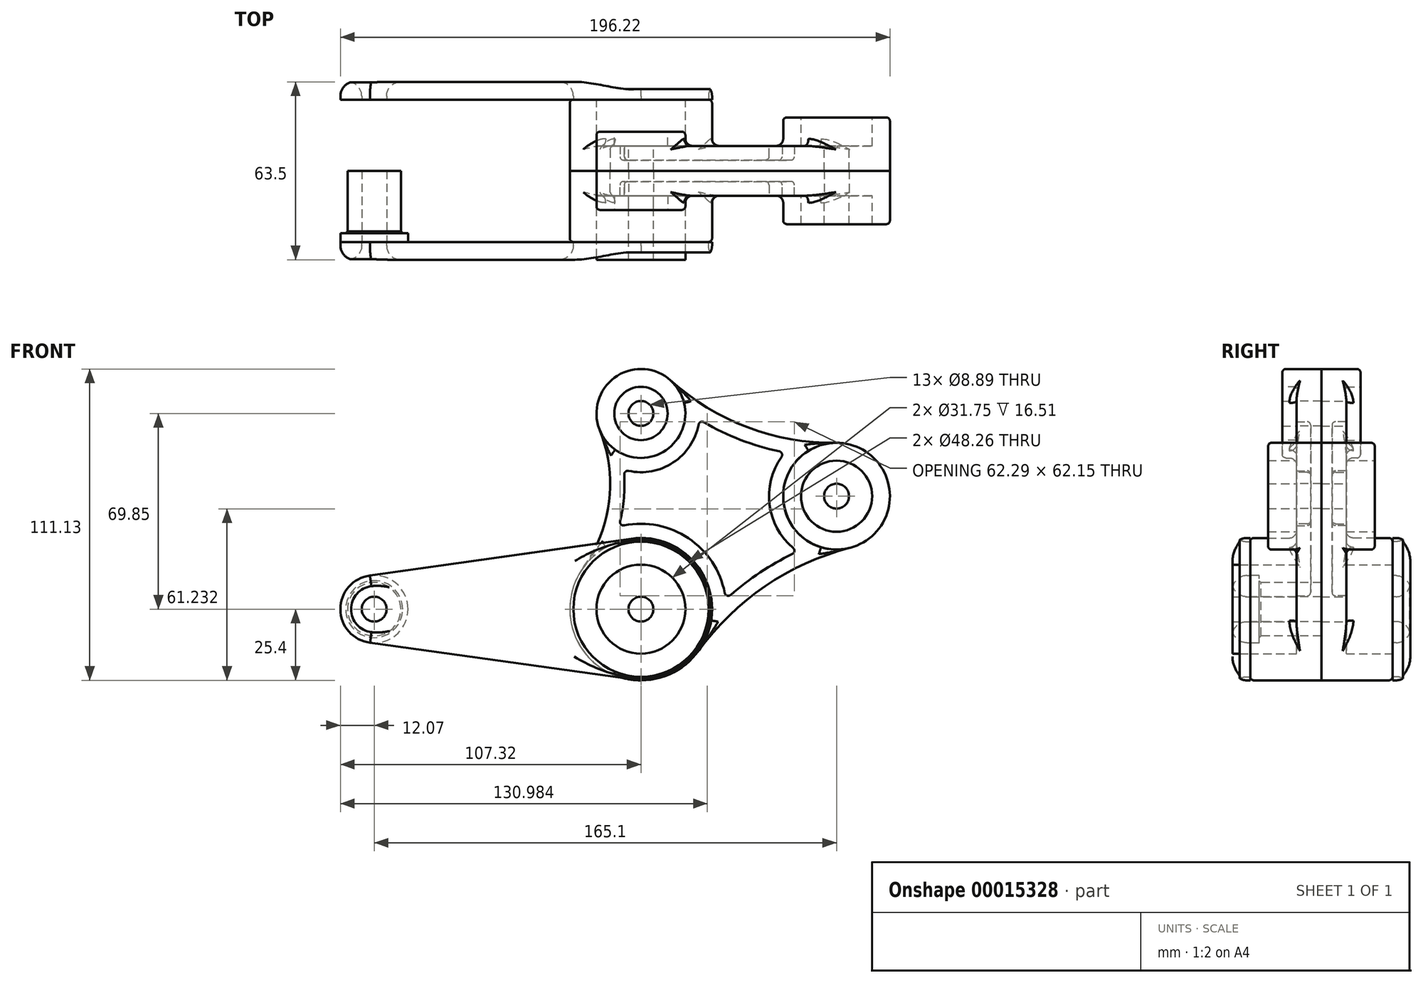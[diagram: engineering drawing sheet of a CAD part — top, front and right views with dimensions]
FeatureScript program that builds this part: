
annotation { "Feature Type Name" : "Feature", "Feature Type Description" : "" }
export const myFeature = defineFeature(function(context is Context, id is Id, definition is map)
    precondition{}
    {
        {
            var Q0;
            Q0=qCreatedBy(makeId("Front.planeOp"),FACE);
            var sketch = newSketch(context, id + "F0", { "sketchPlane" : qUnion([Q0])});
            skCircle(sketch, "E0", {"center": v(0, 0) * mm, "radius": 25.4 * mm});
            skCircle(sketch, "E1", {"center": v(0, 69.85) * mm, "radius": 15.88 * mm});
            skCircle(sketch, "E2", {"center": v(69.85, 40.33) * mm, "radius": 19.05 * mm});
            skLineSegment(sketch, "E3", {"start": v(0, 0) * mm, "end": v(69.85, 40.33) * mm, "construction": true});
            skLineSegment(sketch, "E4", {"start": v(0, 0) * mm, "end": v(74.27, 0) * mm, "construction": true});
            skArc(sketch, "E5", {"start": v(-20.58, 14.89) * mm, "mid": v(-11.3, 38.61) * mm, "end": v(-14.7, 63.85) * mm});
            skArc(sketch, "E6", {"start": v(74.6, 21.88) * mm, "mid": v(44.37, 8.2) * mm, "end": v(20.56, -14.91) * mm});
            skArc(sketch, "E7", {"start": v(10.64, 81.63) * mm, "mid": v(38.02, 64.93) * mm, "end": v(69.6, 59.38) * mm});
            skSolve(sketch);
        }
        {
            var Q0;
            {var subQ0=sQuery(id+"F0.wireOp",EDGE,"E0");var subQ1=sQuery(id+"F0.wireOp",EDGE,"E6");var subQ3=sQuery(id+"F0.wireOp",EDGE,"E5");var subQ4=makeQuery(id+"F0.imprint","INTERSECT",VERTEX,{"derivedFrom":[subQ0,subQ3]});var subQ6=sQuery(id+"F0.wireOp",EDGE,"E1");var subQ9=makeQuery(id+"F0.imprint","INTERSECT",VERTEX,{"derivedFrom":[subQ6,subQ3]});var subQ11=sQuery(id+"F0.wireOp",EDGE,"E2");var subQ13=makeQuery(id+"F0.imprint","INTERSECT",VERTEX,{"derivedFrom":[subQ11,subQ1]});var subQ14=makeQuery(id+"F0.imprint","IMPRINT",EDGE,{"disambiguationData":[TD([[subQ13,1.0]])],"derivedFrom":subQ11});Q0=qUnion([makeQuery(id+"F0.imprint","IMPRINT",FACE,{"disambiguationData":[TD([[makeQuery(id+"F0.imprint","IMPRINT",EDGE,{"disambiguationData":[TD([[subQ4,-1.0]])],"derivedFrom":subQ0}),1.0]])]}),makeQuery(id+"F0.imprint","IMPRINT",FACE,{"disambiguationData":[TD([[makeQuery(id+"F0.imprint","IMPRINT",EDGE,{"disambiguationData":[TD([[subQ9,1.0]])],"derivedFrom":subQ6}),1.0]])]}),makeQuery(id+"F0.imprint","IMPRINT",FACE,{"disambiguationData":[TD([[subQ14,1.0]])]}),makeQuery(id+"F0.imprint","IMPRINT",FACE,{"disambiguationData":[TD([[makeQuery(id+"F0.imprint","IMPRINT",EDGE,{"derivedFrom":subQ3}),-1.0]])]})]);}
            extrude(context, id + "F1", {"entities" : qUnion([Q0]), "depth" : 8.9 * mm});
        }
        {
            var Q0;
            {var subQ0=sQuery(id+"F0.wireOp",EDGE,"E1");var subQ2=makeQuery(id+"F0.imprint","INTERSECT",VERTEX,{"derivedFrom":[subQ0,sQuery(id+"F0.wireOp",EDGE,"E5")]});Q0=makeQuery(id+"F0.imprint","IMPRINT",FACE,{"disambiguationData":[TD([[makeQuery(id+"F0.imprint","IMPRINT",EDGE,{"disambiguationData":[TD([[subQ2,1.0]])],"derivedFrom":subQ0}),1.0]])]});}
            extrude(context, id + "F2", {"entities" : qUnion([Q0]), "operationType" : NewBodyOperationType.ADD, "depth" : 13.97 * mm});
        }
        {
            var Q0;
            {var subQ0=sQuery(id+"F0.wireOp",EDGE,"E2");var subQ2=makeQuery(id+"F0.imprint","INTERSECT",VERTEX,{"derivedFrom":[subQ0,sQuery(id+"F0.wireOp",EDGE,"E6")]});Q0=makeQuery(id+"F0.imprint","IMPRINT",FACE,{"disambiguationData":[TD([[makeQuery(id+"F0.imprint","IMPRINT",EDGE,{"disambiguationData":[TD([[subQ2,1.0]])],"derivedFrom":subQ0}),1.0]])]});}
            extrude(context, id + "F3", {"entities" : qUnion([Q0]), "operationType" : NewBodyOperationType.ADD, "depth" : 19.05 * mm});
        }
        {
            var Q0;
            {var subQ0=sQuery(id+"F0.wireOp",EDGE,"E0");var subQ2=makeQuery(id+"F0.imprint","INTERSECT",VERTEX,{"derivedFrom":[subQ0,sQuery(id+"F0.wireOp",EDGE,"E5")]});Q0=makeQuery(id+"F0.imprint","IMPRINT",FACE,{"disambiguationData":[TD([[makeQuery(id+"F0.imprint","IMPRINT",EDGE,{"disambiguationData":[TD([[subQ2,-1.0]])],"derivedFrom":subQ0}),1.0]])]});}
            extrude(context, id + "F4", {"entities" : qUnion([Q0]), "operationType" : NewBodyOperationType.ADD, "depth" : 25.4 * mm});
        }
        {
            var Q0;
            Q0=makeQuery(id+"F1.opExtrude","CAP_FACE",FACE,{"disambiguationData":[OSD([sQuery(id+"F0.wireOp",EDGE,"E0"),sQuery(id+"F0.wireOp",EDGE,"E1"),sQuery(id+"F0.wireOp",EDGE,"E2"),sQuery(id+"F0.wireOp",EDGE,"E5"),sQuery(id+"F0.wireOp",EDGE,"E6"),sQuery(id+"F0.wireOp",EDGE,"E7")])],"isStart":false});
            var sketch = newSketch(context, id + "F5", { "sketchPlane" : qUnion([Q0])});
            skCircle(sketch, "E8.0", {"center": v(0, 69.85) * mm, "radius": 20.96 * mm});
            skCircle(sketch, "E9.0", {"center": v(69.85, 40.33) * mm, "radius": 24.13 * mm});
            skCircle(sketch, "E10.0", {"center": v(0, 0) * mm, "radius": 30.48 * mm});
            skArc(sketch, "E11.0", {"start": v(-16.46, 11.91) * mm, "mid": v(-6.25, 38) * mm, "end": v(-10, 65.77) * mm});
            skArc(sketch, "E12.0", {"start": v(7.23, 77.86) * mm, "mid": v(36.23, 60.18) * mm, "end": v(69.67, 54.3) * mm});
            skArc(sketch, "E13.0", {"start": v(73.34, 26.8) * mm, "mid": v(41.51, 12.4) * mm, "end": v(16.45, -11.93) * mm});
            skSolve(sketch);
        }
        {
            var Q0;
            {var subQ5=sQuery(id+"F5.wireOp",EDGE,"E12.0");var subQ7=sQuery(id+"F5.wireOp",EDGE,"E8.0");var subQ8=makeQuery(id+"F5.imprint","INTERSECT",VERTEX,{"derivedFrom":[subQ7,subQ5]});Q0=makeQuery(id+"F5.imprint","IMPRINT",FACE,{"disambiguationData":[TD([[makeQuery(id+"F5.imprint","IMPRINT",EDGE,{"disambiguationData":[TD([[subQ8,1.0]])],"derivedFrom":subQ7}),-1.0]])]});}
            extrude(context, id + "F6", {"entities" : qUnion([Q0]), "operationType" : NewBodyOperationType.REMOVE, "oppositeDirection" : true, "depth" : 5.08 * mm});
        }
        {
            var Q0;
            Q0=makeQuery(id+"F4.opExtrude","CAP_FACE",FACE,{"disambiguationData":[OSD([sQuery(id+"F0.wireOp",EDGE,"E0")])],"isStart":false});
            var sketch = newSketch(context, id + "F7", { "sketchPlane" : qUnion([Q0])});
            skCircle(sketch, "E14", {"center": v(0, 0) * mm, "radius": 15.88 * mm});
            skCircle(sketch, "E15.0", {"center": v(0, 69.85) * mm, "radius": 15.88 * mm, "construction": true});
            skCircle(sketch, "E15.1", {"center": v(69.85, 40.33) * mm, "radius": 19.05 * mm, "construction": true});
            skCircle(sketch, "E16", {"center": v(0, 69.85) * mm, "radius": 9.53 * mm});
            skCircle(sketch, "E17", {"center": v(69.85, 40.33) * mm, "radius": 12.7 * mm});
            skSolve(sketch);
        }
        {
            var Q0;
            Q0=makeQuery(id+"F7.imprint","IMPRINT",FACE,{"disambiguationData":[TD([[makeQuery(id+"F7.imprint","IMPRINT",EDGE,{"derivedFrom":sQuery(id+"F7.wireOp",EDGE,"E14")}),1.0]])]});
            var Q1;
            Q1=makeQuery(id+"F7.imprint","IMPRINT",FACE,{"disambiguationData":[TD([[makeQuery(id+"F7.imprint","IMPRINT",EDGE,{"derivedFrom":sQuery(id+"F7.wireOp",EDGE,"E16")}),1.0]])]});
            var Q2;
            Q2=makeQuery(id+"F7.imprint","IMPRINT",FACE,{"disambiguationData":[TD([[makeQuery(id+"F7.imprint","IMPRINT",EDGE,{"derivedFrom":sQuery(id+"F7.wireOp",EDGE,"E17")}),1.0]])]});
            var Q3;
            Q3=makeQuery(id+"F1.opExtrude","CAP_FACE",FACE,{"disambiguationData":[OSD([sQuery(id+"F0.wireOp",EDGE,"E0"),sQuery(id+"F0.wireOp",EDGE,"E1"),sQuery(id+"F0.wireOp",EDGE,"E2"),sQuery(id+"F0.wireOp",EDGE,"E5"),sQuery(id+"F0.wireOp",EDGE,"E6"),sQuery(id+"F0.wireOp",EDGE,"E7")])],"isStart":false});
            extrude(context, id + "F8", {"entities" : qUnion([Q0, Q1, Q2]), "operationType" : NewBodyOperationType.REMOVE, "endBound" : BoundingType.UP_TO_SURFACE, "oppositeDirection" : true, "endBoundEntityFace" : qUnion([Q3]), "depth" : 25.4 * mm});
        }
        {
            var Q0;
            Q0=makeQuery(id+"F8.boolean.opBoolean","COPY",FACE,{"derivedFrom":makeQuery(id+"F8.opExtrude","CAP_FACE",FACE,{"disambiguationData":[OSD([sQuery(id+"F7.wireOp",EDGE,"E17")])],"isStart":false})});
            var sketch = newSketch(context, id + "F9", { "sketchPlane" : qUnion([Q0])});
            skCircle(sketch, "E18.0", {"center": v(0, 69.85) * mm, "radius": 9.53 * mm});
            skCircle(sketch, "E18.1", {"center": v(0, 0) * mm, "radius": 15.88 * mm});
            skCircle(sketch, "E18.2", {"center": v(69.85, 40.33) * mm, "radius": 12.7 * mm});
            skCircle(sketch, "E19", {"center": v(0, 0) * mm, "radius": 4.45 * mm});
            skCircle(sketch, "E20", {"center": v(0, 69.85) * mm, "radius": 4.45 * mm});
            skCircle(sketch, "E21", {"center": v(69.85, 40.33) * mm, "radius": 4.45 * mm});
            skSolve(sketch);
        }
        {
            var Q0;
            Q0=makeQuery(id+"F9.imprint","IMPRINT",FACE,{"disambiguationData":[TD([[makeQuery(id+"F9.imprint","IMPRINT",EDGE,{"derivedFrom":sQuery(id+"F9.wireOp",EDGE,"E20")}),1.0]])]});
            var Q1;
            Q1=makeQuery(id+"F9.imprint","IMPRINT",FACE,{"disambiguationData":[TD([[makeQuery(id+"F9.imprint","IMPRINT",EDGE,{"derivedFrom":sQuery(id+"F9.wireOp",EDGE,"E21")}),1.0]])]});
            var Q2;
            Q2=makeQuery(id+"F9.imprint","IMPRINT",FACE,{"disambiguationData":[TD([[makeQuery(id+"F9.imprint","IMPRINT",EDGE,{"derivedFrom":sQuery(id+"F9.wireOp",EDGE,"E19")}),1.0]])]});
            extrude(context, id + "F10", {"entities" : qUnion([Q0, Q1, Q2]), "operationType" : NewBodyOperationType.REMOVE, "endBound" : BoundingType.THROUGH_ALL, "oppositeDirection" : true, "depth" : 25.4 * mm});
        }
        {
            var Q0;
            Q0=makeQuery(id+"F6.boolean.opBoolean","COPY",FACE,{"derivedFrom":makeQuery(id+"F6.opExtrude","CAP_FACE",FACE,{"disambiguationData":[OSD([sQuery(id+"F5.wireOp",EDGE,"E8.0"),sQuery(id+"F5.wireOp",EDGE,"E9.0"),sQuery(id+"F5.wireOp",EDGE,"E10.0"),sQuery(id+"F5.wireOp",EDGE,"E11.0"),sQuery(id+"F5.wireOp",EDGE,"E12.0"),sQuery(id+"F5.wireOp",EDGE,"E13.0")])],"isStart":false})});
            var Q1;
            Q1=makeQuery(id+"F6.boolean.opBoolean","COPY",EDGE,{"derivedFrom":makeQuery(id+"F6.opExtrude","SWEPT_EDGE",EDGE,{"disambiguationData":[OSD([sQuery(id+"F5.wireOp",EDGE,"E8.0"),sQuery(id+"F5.wireOp",EDGE,"E11.0")])]})});
            var Q2;
            Q2=makeQuery(id+"F6.boolean.opBoolean","COPY",EDGE,{"derivedFrom":makeQuery(id+"F6.opExtrude","SWEPT_EDGE",EDGE,{"disambiguationData":[OSD([sQuery(id+"F5.wireOp",EDGE,"E8.0"),sQuery(id+"F5.wireOp",EDGE,"E12.0")])]})});
            var Q3;
            Q3=makeQuery(id+"F6.boolean.opBoolean","COPY",EDGE,{"derivedFrom":makeQuery(id+"F6.opExtrude","SWEPT_EDGE",EDGE,{"disambiguationData":[OSD([sQuery(id+"F5.wireOp",EDGE,"E9.0"),sQuery(id+"F5.wireOp",EDGE,"E12.0")])]})});
            var Q4;
            Q4=makeQuery(id+"F6.boolean.opBoolean","COPY",EDGE,{"derivedFrom":makeQuery(id+"F6.opExtrude","SWEPT_EDGE",EDGE,{"disambiguationData":[OSD([sQuery(id+"F5.wireOp",EDGE,"E9.0"),sQuery(id+"F5.wireOp",EDGE,"E13.0")])]})});
            var Q5;
            Q5=makeQuery(id+"F6.boolean.opBoolean","COPY",EDGE,{"derivedFrom":makeQuery(id+"F6.opExtrude","SWEPT_EDGE",EDGE,{"disambiguationData":[OSD([sQuery(id+"F5.wireOp",EDGE,"E10.0"),sQuery(id+"F5.wireOp",EDGE,"E13.0")])]})});
            var Q6;
            Q6=makeQuery(id+"F6.boolean.opBoolean","COPY",EDGE,{"derivedFrom":makeQuery(id+"F6.opExtrude","SWEPT_EDGE",EDGE,{"disambiguationData":[OSD([sQuery(id+"F5.wireOp",EDGE,"E10.0"),sQuery(id+"F5.wireOp",EDGE,"E11.0")])]})});
            var Q7;
            Q7=makeQuery(id+"F6.boolean.opBoolean","COPY",EDGE,{"derivedFrom":makeQuery(id+"F6.opExtrude","CAP_EDGE",EDGE,{"disambiguationData":[OSD([sQuery(id+"F5.wireOp",EDGE,"E10.0")])],"isStart":true})});
            var Q8;
            Q8=makeQuery(id+"F1.opExtrude","CAP_EDGE",EDGE,{"disambiguationData":[OSD([sQuery(id+"F0.wireOp",EDGE,"E7")])],"isStart":false});
            var Q9;
            Q9=makeQuery(id+"F1.opExtrude","CAP_EDGE",EDGE,{"disambiguationData":[OSD([sQuery(id+"F0.wireOp",EDGE,"E6")])],"isStart":false});
            var Q10;
            Q10=makeQuery(id+"F1.opExtrude","CAP_EDGE",EDGE,{"disambiguationData":[OSD([sQuery(id+"F0.wireOp",EDGE,"E5")])],"isStart":false});
            var Q11;
            Q11=makeQuery(id+"F4.opExtrude","CAP_EDGE",EDGE,{"disambiguationData":[OSD([sQuery(id+"F0.wireOp",EDGE,"E0")])],"isStart":false});
            var Q12;
            Q12=makeQuery(id+"F3.opExtrude","CAP_EDGE",EDGE,{"disambiguationData":[OSD([sQuery(id+"F0.wireOp",EDGE,"E2")])],"isStart":false});
            var Q13;
            Q13=makeQuery(id+"F2.opExtrude","CAP_EDGE",EDGE,{"disambiguationData":[OSD([sQuery(id+"F0.wireOp",EDGE,"E1")])],"isStart":false});
            fillet(context, id + "F11", {"entities" : qUnion([Q0, Q1, Q2, Q3, Q4, Q5, Q6, Q7, Q8, Q9, Q10, Q11, Q12, Q13]), "radius" : 1.27 * mm, "tangentPropagation" : true, "allowEdgeOverflow" : false});
        }
        {
            var Q0;
            {var subQ0=sQuery(id+"F0.wireOp",EDGE,"E2");Q0=makeQuery(id+"F3.boolean.opBoolean","INTERSECT",EDGE,{"derivedFrom":[makeQuery(id+"F1.opExtrude","CAP_FACE",FACE,{"disambiguationData":[OSD([sQuery(id+"F0.wireOp",EDGE,"E0"),sQuery(id+"F0.wireOp",EDGE,"E1"),subQ0,sQuery(id+"F0.wireOp",EDGE,"E5"),sQuery(id+"F0.wireOp",EDGE,"E6"),sQuery(id+"F0.wireOp",EDGE,"E7")])],"isStart":false}),makeQuery(id+"F3.opExtrude","SWEPT_FACE",FACE,{"disambiguationData":[OSD([subQ0])]})]});}
            var Q1;
            {var subQ0=sQuery(id+"F0.wireOp",EDGE,"E0");Q1=makeQuery(id+"F4.boolean.opBoolean","INTERSECT",EDGE,{"derivedFrom":[makeQuery(id+"F1.opExtrude","CAP_FACE",FACE,{"disambiguationData":[OSD([subQ0,sQuery(id+"F0.wireOp",EDGE,"E1"),sQuery(id+"F0.wireOp",EDGE,"E2"),sQuery(id+"F0.wireOp",EDGE,"E5"),sQuery(id+"F0.wireOp",EDGE,"E6"),sQuery(id+"F0.wireOp",EDGE,"E7")])],"isStart":false}),makeQuery(id+"F4.opExtrude","SWEPT_FACE",FACE,{"disambiguationData":[OSD([subQ0])]})]});}
            var Q2;
            {var subQ0=sQuery(id+"F0.wireOp",EDGE,"E1");Q2=makeQuery(id+"F2.boolean.opBoolean","INTERSECT",EDGE,{"derivedFrom":[makeQuery(id+"F1.opExtrude","CAP_FACE",FACE,{"disambiguationData":[OSD([sQuery(id+"F0.wireOp",EDGE,"E0"),subQ0,sQuery(id+"F0.wireOp",EDGE,"E2"),sQuery(id+"F0.wireOp",EDGE,"E5"),sQuery(id+"F0.wireOp",EDGE,"E6"),sQuery(id+"F0.wireOp",EDGE,"E7")])],"isStart":false}),makeQuery(id+"F2.opExtrude","SWEPT_FACE",FACE,{"disambiguationData":[OSD([subQ0])]})]});}
            fillet(context, id + "F12", {"entities" : qUnion([Q0, Q1, Q2]), "radius" : 2.54 * mm, "tangentPropagation" : true, "allowEdgeOverflow" : false});
        }
        {
            var Q0;
            Q0=makeQuery(id+"F1.opExtrude","SWEPT_BODY",BODY,{"disambiguationData":[OSD([sQuery(id+"F0.wireOp",EDGE,"E0"),sQuery(id+"F0.wireOp",EDGE,"E1"),sQuery(id+"F0.wireOp",EDGE,"E2"),sQuery(id+"F0.wireOp",EDGE,"E5"),sQuery(id+"F0.wireOp",EDGE,"E6"),sQuery(id+"F0.wireOp",EDGE,"E7")])]});
            var Q1;
            Q1=qCreatedBy(makeId("Front.planeOp"),FACE);
            mirror(context, id + "F13", {"entities" : qUnion([Q0]), "mirrorPlane" : qUnion([Q1])});
        }
        {
            var Q0;
            Q0=makeQuery(id+"F8.boolean.opBoolean","COPY",FACE,{"derivedFrom":makeQuery(id+"F8.opExtrude","CAP_FACE",FACE,{"disambiguationData":[OSD([sQuery(id+"F7.wireOp",EDGE,"E16")])],"isStart":false})});
            var sketch = newSketch(context, id + "F14", { "sketchPlane" : qUnion([Q0])});
            skCircle(sketch, "E22.0.0", {"center": v(0, 69.85) * mm, "radius": 9.53 * mm});
            skSolve(sketch);
        }
        {
            var Q0;
            Q0=makeQuery(id+"F14.imprint","IMPRINT",FACE,{"disambiguationData":[TD([[makeQuery(id+"F14.imprint","IMPRINT",EDGE,{"derivedFrom":sQuery(id+"F14.wireOp",EDGE,"E22.0.0")}),-1.0]])]});
            var Q1;
            Q1=makeQuery(id+"F2.opExtrude","CAP_FACE",FACE,{"disambiguationData":[OSD([sQuery(id+"F0.wireOp",EDGE,"E1")])],"isStart":false});
            extrude(context, id + "F15", {"entities" : qUnion([Q0]), "endBound" : BoundingType.UP_TO_SURFACE, "endBoundEntityFace" : qUnion([Q1]), "depth" : 25.4 * mm});
        }
        {
            var Q0;
            Q0=makeQuery(id+"F8.boolean.opBoolean","COPY",FACE,{"derivedFrom":makeQuery(id+"F8.opExtrude","CAP_FACE",FACE,{"disambiguationData":[OSD([sQuery(id+"F7.wireOp",EDGE,"E17")])],"isStart":false})});
            var Q1;
            Q1=makeQuery(id+"F3.opExtrude","CAP_FACE",FACE,{"disambiguationData":[OSD([sQuery(id+"F0.wireOp",EDGE,"E2")])],"isStart":false});
            extrude(context, id + "F16", {"entities" : qUnion([Q0]), "endBound" : BoundingType.UP_TO_SURFACE, "endBoundEntityFace" : qUnion([Q1]), "depth" : 25.4 * mm});
        }
        {
            var Q0;
            Q0=makeQuery(id+"F8.boolean.opBoolean","COPY",FACE,{"derivedFrom":makeQuery(id+"F8.opExtrude","CAP_FACE",FACE,{"disambiguationData":[OSD([sQuery(id+"F7.wireOp",EDGE,"E14")])],"isStart":false})});
            var sketch = newSketch(context, id + "F17", { "sketchPlane" : qUnion([Q0])});
            skCircle(sketch, "E23.0", {"center": v(0, 0) * mm, "radius": 4.45 * mm});
            skCircle(sketch, "E23.1", {"center": v(0, 0) * mm, "radius": 15.88 * mm});
            skSolve(sketch);
        }
        {
            var Q0;
            Q0=makeQuery(id+"F17.imprint","IMPRINT",FACE,{"disambiguationData":[TD([[makeQuery(id+"F17.imprint","IMPRINT",EDGE,{"derivedFrom":sQuery(id+"F17.wireOp",EDGE,"E23.0")}),-1.0]])]});
            var Q1;
            Q1=makeQuery(id+"F4.opExtrude","CAP_FACE",FACE,{"disambiguationData":[OSD([sQuery(id+"F0.wireOp",EDGE,"E0")])],"isStart":false});
            extrude(context, id + "F18", {"entities" : qUnion([Q0]), "endBound" : BoundingType.UP_TO_SURFACE, "endBoundEntityFace" : qUnion([Q1]), "depth" : 25.4 * mm});
        }
        {
            var Q0;
            Q0=qCreatedBy(makeId("Top.planeOp"),FACE);
            var sketch = newSketch(context, id + "F19", { "sketchPlane" : qUnion([Q0])});
            skLineSegment(sketch, "E24", {"start": v(-90.8, 0) * mm, "end": v(-90.8, -25.4) * mm});
            skLineSegment(sketch, "E25", {"start": v(-90.8, -25.4) * mm, "end": v(-83.19, -25.4) * mm});
            skLineSegment(sketch, "E26", {"start": v(-83.19, -25.4) * mm, "end": v(-83.19, -22.23) * mm});
            skLineSegment(sketch, "E27", {"start": v(-83.19, -22.23) * mm, "end": v(-85.1, -22.23) * mm});
            skLineSegment(sketch, "E28", {"start": v(-85.1, -22.23) * mm, "end": v(-85.73, -21.6) * mm});
            skLineSegment(sketch, "E29", {"start": v(-85.73, -21.6) * mm, "end": v(-85.73, 0) * mm});
            skLineSegment(sketch, "E30", {"start": v(-85.73, 0) * mm, "end": v(-90.8, 0) * mm});
            skLineSegment(sketch, "E31.0", {"start": v(24.13, -25.4) * mm, "end": v(-24.13, -25.4) * mm});
            skLineSegment(sketch, "E32", {"start": v(-95.25, -25.4) * mm, "end": v(-95.25, 0) * mm, "construction": true});
            skSolve(sketch);
        }
        {
            var Q0;
            Q0=makeQuery(id+"F19.imprint","IMPRINT",FACE,{"disambiguationData":[TD([[makeQuery(id+"F19.imprint","IMPRINT",EDGE,{"derivedFrom":sQuery(id+"F19.wireOp",EDGE,"E24")}),1.0]])]});
            var Q1;
            Q1=sQuery(id+"F19.wireOp",EDGE,"E32");
            revolve(context, id + "F20", {"entities" : qUnion([Q0]), "axis" : qUnion([Q1]), "revolveType" : RevolveType.FULL});
        }
        {
            var Q0;
            Q0=makeQuery(id+"F4.opExtrude","CAP_FACE",FACE,{"disambiguationData":[OSD([sQuery(id+"F0.wireOp",EDGE,"E0")])],"isStart":false});
            var sketch = newSketch(context, id + "F21", { "sketchPlane" : qUnion([Q0])});
            skCircle(sketch, "E33.0", {"center": v(-95.25, 0) * mm, "radius": 12.07 * mm});
            skArc(sketch, "E34.0", {"start": v(-96.74, 11.97) * mm, "mid": v(-107.31, -0.03) * mm, "end": v(-96.7, -11.98) * mm});
            skCircle(sketch, "E34.1", {"center": v(-95.25, 0) * mm, "radius": 4.45 * mm});
            skCircle(sketch, "E35.2", {"center": v(0, 0) * mm, "radius": 25.4 * mm});
            skArc(sketch, "E36.2", {"start": v(-6.92, -24.44) * mm, "mid": v(25.34, -1.72) * mm, "end": v(-3.56, 25.15) * mm});
            skCircle(sketch, "E36.3", {"center": v(0, 0) * mm, "radius": 4.45 * mm});
            skLineSegment(sketch, "E37", {"start": v(-96.74, 11.97) * mm, "end": v(-3.56, 25.15) * mm});
            skLineSegment(sketch, "E38", {"start": v(-96.7, -11.98) * mm, "end": v(0, -25.4) * mm});
            skSolve(sketch);
        }
        {
            var Q0;
            {var subQ0=sQuery(id+"F0.wireOp",EDGE,"E0");Q0=makeQuery(id+"F21.imprint","IMPRINT",FACE,{"disambiguationData":[TD([[makeQuery(id+"F21.imprint","IMPRINT",EDGE,{"derivedFrom":makeQuery(id+"F11.opFillet","BLEND_EDGE",EDGE,{"blendedFrom":[makeQuery(id+"F4.opExtrude","CAP_EDGE",EDGE,{"disambiguationData":[OSD([subQ0])],"isStart":false}),makeQuery(id+"F4.opExtrude","CAP_FACE",FACE,{"disambiguationData":[OSD([subQ0])],"isStart":false})],"blendedInto":[makeQuery(id+"F4.opExtrude","CAP_FACE",FACE,{"disambiguationData":[OSD([subQ0])],"isStart":false})]})}),-1.0]])]});}
            var Q1;
            {var subQ0=sQuery(id+"F21.wireOp",EDGE,"E38");var subQ1=sQuery(id+"F21.wireOp",EDGE,"E35.2");var subQ3=makeQuery(id+"F21.imprint","INTERSECT",VERTEX,{"disambiguationData":[OD(0.0)],"derivedFrom":[subQ1,subQ0]});Q1=makeQuery(id+"F21.imprint","IMPRINT",FACE,{"disambiguationData":[TD([[makeQuery(id+"F21.imprint","IMPRINT",EDGE,{"disambiguationData":[TD([[subQ3,1.0]])],"derivedFrom":subQ1}),1.0]])]});}
            var Q2;
            Q2=makeQuery(id+"F21.imprint","IMPRINT",FACE,{"disambiguationData":[TD([[makeQuery(id+"F21.imprint","IMPRINT",EDGE,{"derivedFrom":sQuery(id+"F21.wireOp",EDGE,"E34.1")}),-1.0]])]});
            var Q3;
            {var subQ5=sQuery(id+"F21.wireOp",EDGE,"E37");Q3=makeQuery(id+"F21.imprint","IMPRINT",FACE,{"disambiguationData":[TD([[makeQuery(id+"F21.imprint","IMPRINT",EDGE,{"derivedFrom":subQ5}),-1.0]])]});}
            var Q4;
            Q4=makeQuery(id+"F21.imprint","IMPRINT",FACE,{"disambiguationData":[TD([[makeQuery(id+"F21.imprint","IMPRINT",EDGE,{"derivedFrom":makeQuery(id+"F8.boolean.opBoolean","COPY",EDGE,{"derivedFrom":makeQuery(id+"F8.opExtrude","CAP_EDGE",EDGE,{"disambiguationData":[OSD([sQuery(id+"F7.wireOp",EDGE,"E14")])],"isStart":true})})}),-1.0]])]});
            var Q5;
            Q5=makeQuery(id+"F21.imprint","IMPRINT",FACE,{"disambiguationData":[TD([[makeQuery(id+"F21.imprint","IMPRINT",EDGE,{"derivedFrom":sQuery(id+"F21.wireOp",EDGE,"E36.3")}),-1.0]])]});
            extrude(context, id + "F22", {"entities" : qUnion([Q0, Q1, Q2, Q3, Q4, Q5]), "depth" : 6.35 * mm});
        }
        {
            var Q0;
            Q0=makeQuery(id+"F22.opExtrude","CAP_FACE",FACE,{"disambiguationData":[OSD([sQuery(id+"F21.wireOp",EDGE,"E35.2"),sQuery(id+"F21.wireOp",EDGE,"E33.0"),sQuery(id+"F21.wireOp",EDGE,"E34.1"),sQuery(id+"F21.wireOp",EDGE,"E36.3"),sQuery(id+"F21.wireOp",EDGE,"E37"),sQuery(id+"F21.wireOp",EDGE,"E38")])],"isStart":false});
            fillet(context, id + "F23", {"entities" : qUnion([Q0]), "radius" : 5.08 * mm, "tangentPropagation" : true, "allowEdgeOverflow" : false});
        }
        {
            var Q0;
            Q0=makeQuery(id+"F22.opExtrude","SWEPT_BODY",BODY,{"disambiguationData":[OSD([sQuery(id+"F21.wireOp",EDGE,"E35.2"),sQuery(id+"F21.wireOp",EDGE,"E33.0"),sQuery(id+"F21.wireOp",EDGE,"E34.1"),sQuery(id+"F21.wireOp",EDGE,"E36.3"),sQuery(id+"F21.wireOp",EDGE,"E37"),sQuery(id+"F21.wireOp",EDGE,"E38")])]});
            var Q1;
            Q1=qCreatedBy(makeId("Front.planeOp"),FACE);
            mirror(context, id + "F24", {"entities" : qUnion([Q0]), "mirrorPlane" : qUnion([Q1])});
        }
    });
